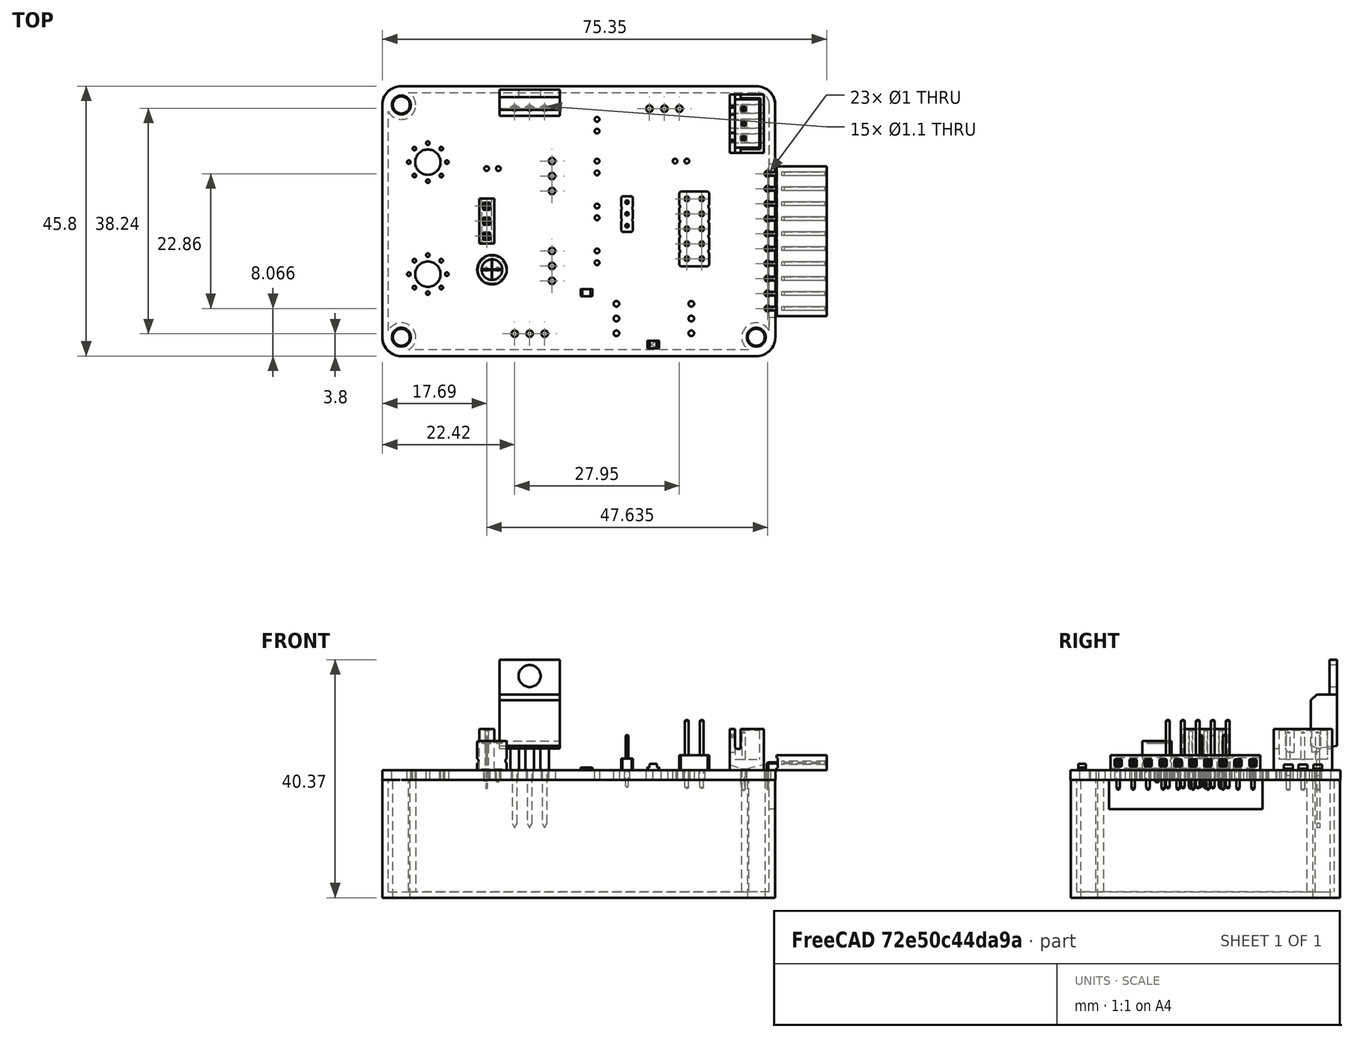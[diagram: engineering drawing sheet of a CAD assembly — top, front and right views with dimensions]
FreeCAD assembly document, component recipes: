
FREECAD ASSEMBLY — COMPONENT RECIPES ("ELLoadSimplePowerCase")

This assembly document has 2 components, labeled P0..P1 below (a component is one placed body or linked part). 1 of them carries a construction recipe — the FreeCAD feature program that regenerates the part from scratch, quoted from this document or its linked companion documents; the rest are supplied as boundary geometry only. No exploded tour is included for this assembly.
COMPONENT P0 — geometry summary ("EL-Load-V2-Simple-Power"; no construction recipe available for this part):
  bounding box: 75.4 x 45.8 x 28.5 mm
  tessellated surface: 9,716 triangles
  volume: 45585940273129844082958573213864865076099481602929601951797735244921485286110992419918130188470190080 mm^3 (46305103217719325866622822304091003216084093823702966931440907959348624955941659054119829228224512% of its bounding box)
COMPONENT P1 — recipe-attached ("Body", modeled in this document).
Construction recipe (the document's own serialized feature program — sketch geometry with constraints, then the solid features built on it; lengths are millimeters unless a unit is written):

FEATURE [Sketcher::SketchObject] Sketch
  FullyConstrained = true
  MapMode = 5
  Support = -> [XY_Plane]
  sketch-geometry (15):
    g0: ArcOfCircle CenterX=-30.3 CenterY=19.825 CenterZ=0 NormalX=0 NormalY=0 NormalZ=1 AngleXU=0 Radius=3 StartAngle=1.5708 EndAngle=3.14159
    g1: LineSegment StartX=-30.3 StartY=22.825 StartZ=0 EndX=30.3 EndY=22.825 EndZ=0
    g2: ArcOfCircle CenterX=30.3 CenterY=19.825 CenterZ=0 NormalX=0 NormalY=0 NormalZ=1 AngleXU=0 Radius=3 StartAngle=4e-16 EndAngle=1.5708
    g3: LineSegment StartX=33.3 StartY=19.825 StartZ=0 EndX=33.3 EndY=-19.825 EndZ=0
    g4: ArcOfCircle CenterX=30.3 CenterY=-19.825 CenterZ=0 NormalX=0 NormalY=0 NormalZ=1 AngleXU=0 Radius=3 StartAngle=4.71239 EndAngle=6.28319
    g5: LineSegment StartX=30.3 StartY=-22.825 StartZ=0 EndX=-30.3 EndY=-22.825 EndZ=0
    g6: ArcOfCircle CenterX=-30.3 CenterY=-19.825 CenterZ=0 NormalX=0 NormalY=0 NormalZ=1 AngleXU=0 Radius=3 StartAngle=3.14159 EndAngle=4.71239
    g7: LineSegment StartX=-33.3 StartY=-19.825 StartZ=0 EndX=-33.3 EndY=19.825 EndZ=0
    g8: GeomPoint X=-33.3 Y=22.825 Z=0
    g9: GeomPoint X=33.3 Y=-22.825 Z=0
    g10: Circle CenterX=-30.1 CenterY=19.7 CenterZ=0 NormalX=0 NormalY=0 NormalZ=1 AngleXU=0 Radius=1.45
    g11: Circle CenterX=-30.1 CenterY=-19.7 CenterZ=0 NormalX=0 NormalY=0 NormalZ=1 AngleXU=0 Radius=1.45
    g12: Circle CenterX=30.1 CenterY=-19.7 CenterZ=0 NormalX=0 NormalY=0 NormalZ=1 AngleXU=0 Radius=1.45
    g13: LineSegment StartX=-30.1 StartY=19.7 StartZ=0 EndX=-30.1 EndY=-19.7 EndZ=0
    g14: LineSegment StartX=-30.1 StartY=-19.7 StartZ=0 EndX=30.1 EndY=-19.7 EndZ=0
  constraints (34):
    c: Tangent(g0,g1) = 1.5708
    c: Tangent(g1,g2) = 1.5708
    c: Tangent(g2,g3) = 1.5708
    c: Tangent(g3,g4) = 1.5708
    c: Tangent(g4,g5) = 1.5708
    c: Tangent(g5,g6) = 1.5708
    c: Tangent(g6,g7) = 1.5708
    c: Tangent(g7,g0) = 1.5708
    c: Horizontal(g1)
    c: Horizontal(g5)
    c: Vertical(g3)
    c: Vertical(g7)
    c: Equal(g0,g2)
    c: Equal(g2,g4)
    c: Equal(g4,g6)
    c: PointOnObject(g8,g1)
    c: PointOnObject(g8,g7)
    c: PointOnObject(g9,g3)
    c: PointOnObject(g9,g5)
    c: Symmetric(g0,g4,g-1)
    c: DistanceX(g0,g2) = 66.6
    c: DistanceY(g5,g0) = 45.65
    c: Coincident(g13,g10)
    c: Coincident(g13,g11)
    c: Coincident(g14,g11)
    c: Coincident(g14,g12)
    c: DistanceY(g11,g10) = 39.4
    c: Symmetric(g10,g11,g-1)
    c: Symmetric(g11,g12,g-2)
    c: DistanceX(g14,g14) = 60.2
    c: Diameter(g12) = 2.9
    c: Equal(g12,g11)
    c: Equal(g11,g10)
    c: Radius(g2) = 3
FEATURE [PartDesign::Pad] Pad
  Direction = (0,0,1)
  Length = 20
  Length2 = 10
  Profile = -> Sketch
  ReferenceAxis = -> Sketch [N_Axis]
  Reversed = true
  Type = 0
FEATURE [PartDesign::Thickness] Thickness
  Base = -> Pad [Face12]
  BaseFeature = -> Pad
  Intersection = true
  Join = 1
  Mode = 1
  Reversed = true
  SupportTransform = false
  Value = 1
FEATURE [PartDesign::Plane] DatumPlane
  Length = 78.1412
  MapMode = 5
  ResizeMode = 0
  Support = -> [Thickness]
  Width = 61.5412
FEATURE [PartDesign::Plane] DatumPlane001
  Length = 60
  MapMode = 5
  Placement = pos=(33.3,0,0) rot=(0.57735,0.57735,0.57735;2.0944rad)
  ResizeMode = 0
  Support = -> [Thickness]
  Width = 60
FEATURE [Sketcher::SketchObject] Sketch001
  FullyConstrained = true
  MapMode = 5
  Placement = pos=(33.3,0,0) rot=(0.57735,0.57735,0.57735;2.0944rad)
  Support = -> [DatumPlane001]
  sketch-geometry (4):
    g0: LineSegment StartX=-16.35 StartY=0 StartZ=0 EndX=9.65 EndY=0 EndZ=0
    g1: LineSegment StartX=9.65 StartY=0 StartZ=0 EndX=9.65 EndY=-5 EndZ=0
    g2: LineSegment StartX=9.65 StartY=-5 StartZ=0 EndX=-16.35 EndY=-5 EndZ=0
    g3: LineSegment StartX=-16.35 StartY=-5 StartZ=0 EndX=-16.35 EndY=0 EndZ=0
  constraints (12):
    c: Coincident(g0,g1)
    c: Coincident(g1,g2)
    c: Coincident(g2,g3)
    c: Coincident(g3,g0)
    c: Horizontal(g0)
    c: Horizontal(g2)
    c: Vertical(g1)
    c: Vertical(g3)
    c: PointOnObject(g0,g-1)
    c: DistanceX(g2,g2) = 26
    c: DistanceY(g1,g1) = 5
    c: DistanceX(g-1,g0) = 9.65
FEATURE [PartDesign::Pocket] Pocket
  BaseFeature = -> Thickness
  Direction = (-1,0,0)
  Length = 5
  Length2 = 5
  Profile = -> Sketch001
  ReferenceAxis = -> Sketch001 [N_Axis]
  Type = 0
FEATURE [PartDesign::Body] Body
  Group = -> [Sketch,Pad,Thickness,DatumPlane,DatumPlane001,Sketch001,Pocket]
  Origin = -> Origin
  Placement = pos=(149.3,-94,-1.6) rot=(0,0,1;0rad)
  Tip = -> Pocket
PROVENANCE & LICENSES
A FreeCAD (.FCStd) document from a public repository crawl; recipes are the document's own serialized feature recipes (and, for linked parts, companion documents' recipes).
License: as declared in the source repository (recorded in the dataset sidecar).
